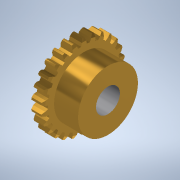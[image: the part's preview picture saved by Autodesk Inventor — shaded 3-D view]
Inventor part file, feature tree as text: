
AUTODESK INVENTOR PART (.ipt)
format: ipt  version: 2020.2 (Build 242310000, 310)  size: 398,848 bytes
history: native  units: mm
features: extrude x1, sketch x1
ambient origin geometry x8: Origin, YZ Plane, XZ Plane, XY Plane, X Axis, Y Axis, Z Axis, Center Point
bodies: Volumenkörper1 (feature_tree)
feature tree (2):
  extrude  "Extrusion1"  TaperAngle=0.0deg  [1 undecoded]
  sketch  "Sketch3"  dims[d8=4.0mm d9=0.0mm d10=0.0mm]
note: 1 required parameter value undecoded (feature->parameter linkage not recoverable at this tier; creation-order binding heuristic only, values carry confidence <= 0.55)
